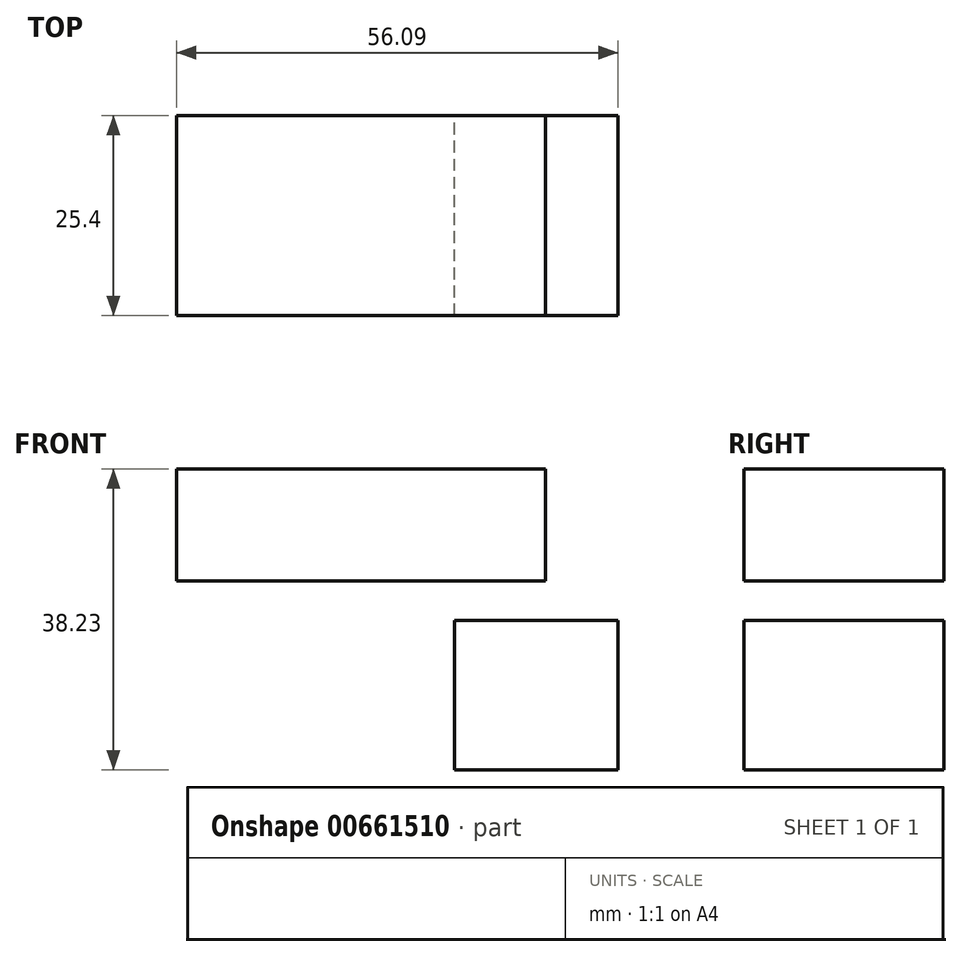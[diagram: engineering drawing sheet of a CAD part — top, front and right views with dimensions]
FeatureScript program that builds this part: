
annotation { "Feature Type Name" : "Feature", "Feature Type Description" : "" }
export const myFeature = defineFeature(function(context is Context, id is Id, definition is map)
    precondition{}
    {
        {
            var Q0;
            Q0=qCreatedBy(makeId("Front.planeOp"),FACE);
            var sketch = newSketch(context, id + "F0", { "sketchPlane" : qUnion([Q0])});
            skLineSegment(sketch, "E0.bottom", {"start": v(2.02, 0) * mm, "end": v(22.76, 0) * mm});
            skLineSegment(sketch, "E0.top", {"start": v(2.02, -19.02) * mm, "end": v(22.76, -19.02) * mm});
            skLineSegment(sketch, "E0.left", {"start": v(2.02, 0) * mm, "end": v(2.02, -19.02) * mm});
            skLineSegment(sketch, "E0.right", {"start": v(22.76, 0) * mm, "end": v(22.76, -19.02) * mm});
            skLineSegment(sketch, "E1.bottom", {"start": v(13.54, 5) * mm, "end": v(-33.33, 5) * mm});
            skLineSegment(sketch, "E1.top", {"start": v(13.54, 19.2) * mm, "end": v(-33.33, 19.2) * mm});
            skLineSegment(sketch, "E1.left", {"start": v(13.54, 5) * mm, "end": v(13.54, 19.2) * mm});
            skLineSegment(sketch, "E1.right", {"start": v(-33.33, 5) * mm, "end": v(-33.33, 19.2) * mm});
            skSolve(sketch);
        }
        {
            var Q0;
            Q0 = qSketchRegion(id + "F0", true);
            extrude(context, id + "F1", {"entities" : qUnion([Q0]), "depth" : 25.4 * mm, "offsetDistance" : 25.4 * mm});
        }
    });
